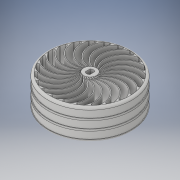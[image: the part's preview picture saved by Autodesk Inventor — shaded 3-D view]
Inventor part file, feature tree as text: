
AUTODESK INVENTOR PART (.ipt)
format: ipt  version: 2019.4 (Build 234330000, 330)  size: 809,984 bytes
history: native  units: mm
features: fillet x14, sketch x4, extrude x4, plane x2, emboss x1, pattern_circular x1
ambient origin geometry x8: Origin, YZ Plane, XZ Plane, XY Plane, X Axis, Y Axis, Z Axis, Center Point
bodies: Solid1 (feature_tree)
feature tree (26):
  sketch  "Sketch1"  dims[d1=65.0mm d15=10.69mm]
  extrude  "Extrusion3"  Depth=10.69mm
  plane  "Work Plane1"
  sketch  "Sketch2"  dims[d16=0.69mm d29=230.0mm d31=360.0deg]
  extrude  "Extrusion2"  Depth=230.0mm TaperAngle=360.0deg
  extrude  "Extrusion4"  Depth=3.8665mm
  sketch  "Sketch3"  dims[d35=5.94mm d36=0.0mm d40=3.8665mm]
  extrude  "Extrusion5"  Depth=25.0mm TaperAngle=0.0deg
  fillet  "Fillet1"  Radius=26.0mm
  plane  "Work Plane2"
  emboss  "Emboss1"
  pattern_circular  "Circular Pattern1"  [2 undecoded]
  fillet  "Fillet2"  Radius=1.0mm
  fillet  "Fillet3"  Radius=34.5mm
  fillet  "Fillet4"  Radius=6.0mm
  fillet  "Fillet5"  Radius=2.0mm
  fillet  "Fillet6"  Radius=1.5mm
  fillet  "Fillet7"  Radius=1.5mm
  fillet  "Fillet8"  Radius=6.0mm
  fillet  "Fillet9"  Radius=2.0mm
  fillet  "Fillet10"  Radius=6.0mm
  fillet  "Fillet11"  Radius=0.5mm
  fillet  "Fillet12"  Radius=40.0mm
  fillet  "Fillet13"  Radius=1.0mm
  fillet  "Fillet14"  Radius=1.0mm
  sketch  "Sketch5"  dims[d41=10.0mm d42=0.0mm d43=25.0mm d44=0.0mm d45=26.0mm d46=0.0mm d47=50.5mm d48=0.0mm d49=1.0mm d50=34.5mm d51=6.0mm d52=2.0mm d53=1.5mm d54=1.5mm d55=6.0mm d56=2.0mm d57=6.0mm d58=0.5mm d59=0.0mm d60=40.0mm d61=360.0deg d63=1.0mm d64=1.0mm d65=1.0mm d66=1.0mm d67=1.0mm d68=1.0mm d69=1.0mm d70=2.0mm d71=2.0mm d72=1.0mm d73=1.0mm d74=1.0mm d75=4.110186mm d76=1.0mm]
note: 2 required parameter values undecoded (feature->parameter linkage not recoverable at this tier; creation-order binding heuristic only, values carry confidence <= 0.55)
